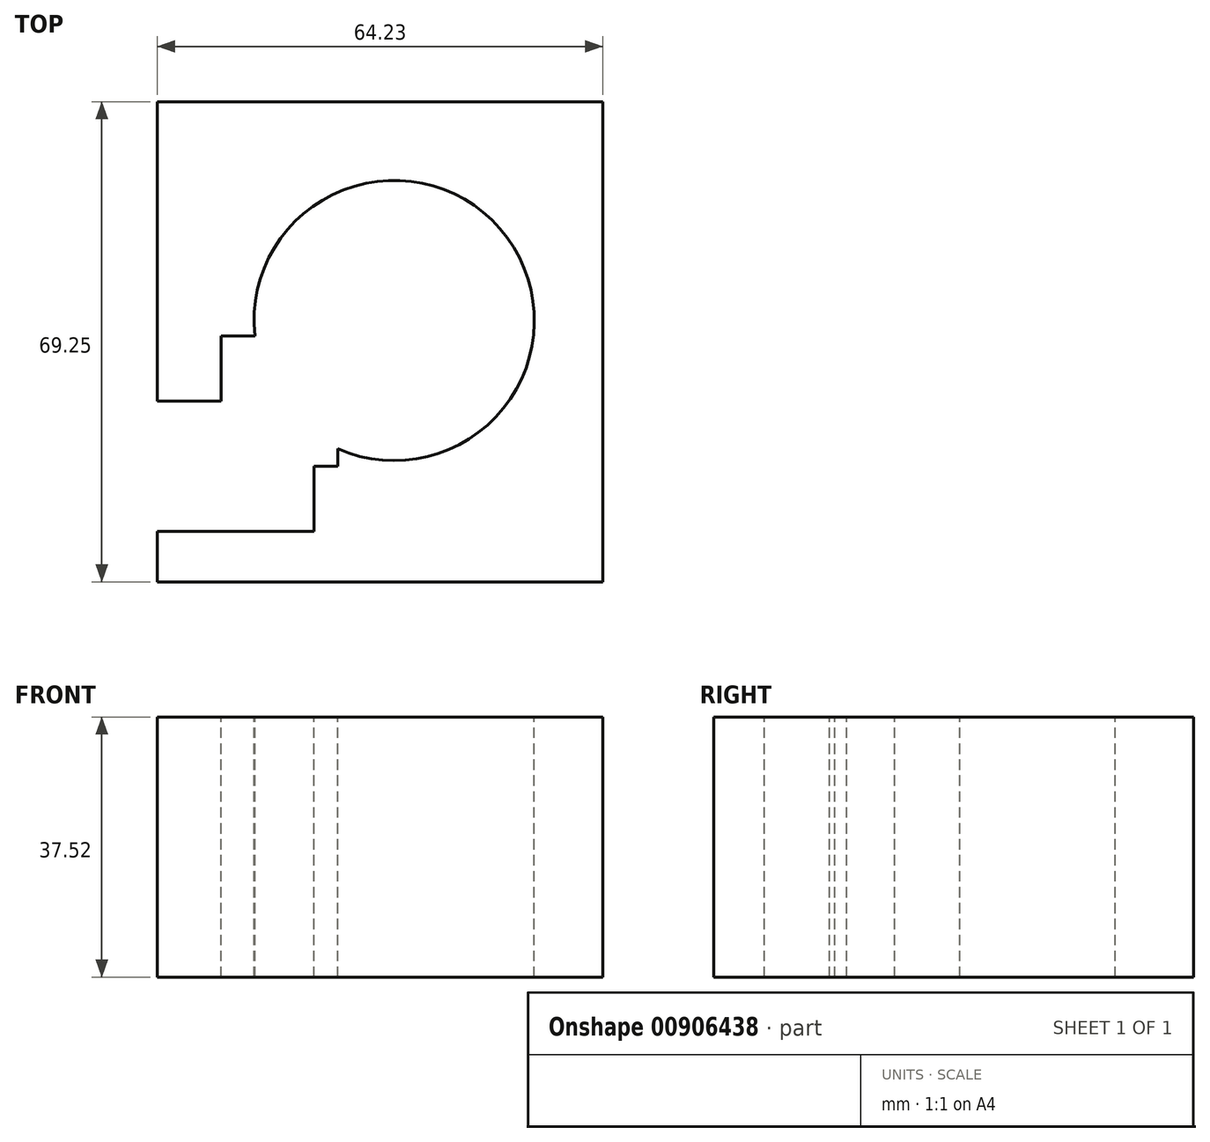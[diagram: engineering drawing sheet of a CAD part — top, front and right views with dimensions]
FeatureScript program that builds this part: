
annotation { "Feature Type Name" : "Feature", "Feature Type Description" : "" }
export const myFeature = defineFeature(function(context is Context, id is Id, definition is map)
    precondition{}
    {
        {
            var Q0;
            Q0=qCreatedBy(makeId("Top.planeOp"),FACE);
            var sketch = newSketch(context, id + "F0", { "sketchPlane" : qUnion([Q0])});
            skLineSegment(sketch, "E0.bottom", {"start": v(-34.15, 31.55) * mm, "end": v(30.08, 31.55) * mm});
            skLineSegment(sketch, "E0.top", {"start": v(-34.15, -37.7) * mm, "end": v(30.08, -37.7) * mm});
            skLineSegment(sketch, "E0.left", {"start": v(-34.15, 31.55) * mm, "end": v(-34.15, -37.7) * mm});
            skLineSegment(sketch, "E0.right", {"start": v(30.08, 31.55) * mm, "end": v(30.08, -37.7) * mm});
            skSolve(sketch);
        }
        {
            var Q0;
            Q0 = qSketchRegion(id + "F0", true);
            extrude(context, id + "F1", {"entities" : qUnion([Q0]), "depth" : 37.52 * mm, "offsetDistance" : 25.4 * mm});
        }
        {
            var Q0;
            Q0=makeQuery(id+"F1.opExtrude","CAP_FACE",FACE,{"disambiguationData":[OSD([sQuery(id+"F0.wireOp",EDGE,"E0.bottom"),sQuery(id+"F0.wireOp",EDGE,"E0.top"),sQuery(id+"F0.wireOp",EDGE,"E0.left"),sQuery(id+"F0.wireOp",EDGE,"E0.right")])],"isStart":false});
            var sketch = newSketch(context, id + "F2", { "sketchPlane" : qUnion([Q0])});
            skCircle(sketch, "E1", {"center": v(0, 0) * mm, "radius": 20.22 * mm});
            skSolve(sketch);
        }
        {
            var Q0;
            Q0 = qSketchRegion(id + "F2", true);
            extrude(context, id + "F3", {"entities" : qUnion([Q0]), "operationType" : NewBodyOperationType.REMOVE, "oppositeDirection" : true, "depth" : 93.56 * mm, "offsetDistance" : 25.4 * mm});
        }
        {
            var Q0;
            Q0=makeQuery(id+"F1.opExtrude","CAP_FACE",FACE,{"disambiguationData":[OSD([sQuery(id+"F0.wireOp",EDGE,"E0.bottom"),sQuery(id+"F0.wireOp",EDGE,"E0.top"),sQuery(id+"F0.wireOp",EDGE,"E0.left"),sQuery(id+"F0.wireOp",EDGE,"E0.right")])],"isStart":false});
            var sketch = newSketch(context, id + "F4", { "sketchPlane" : qUnion([Q0])});
            skLineSegment(sketch, "E2.bottom", {"start": v(-11.54, -30.39) * mm, "end": v(-38.41, -30.39) * mm});
            skLineSegment(sketch, "E2.top", {"start": v(-11.54, -11.6) * mm, "end": v(-38.41, -11.6) * mm});
            skLineSegment(sketch, "E2.left", {"start": v(-11.54, -30.39) * mm, "end": v(-11.54, -11.6) * mm});
            skLineSegment(sketch, "E2.right", {"start": v(-38.41, -30.39) * mm, "end": v(-38.41, -11.6) * mm});
            skPoint(sketch, "E2.middle", {"position": v(-24.98, -21) * mm});
            skLineSegment(sketch, "E3.bottom", {"start": v(-38.41, -21) * mm, "end": v(-11.54, -21) * mm});
            skLineSegment(sketch, "E3.top", {"start": v(-38.41, -21) * mm, "end": v(-11.54, -21) * mm});
            skLineSegment(sketch, "E3.left", {"start": v(-38.41, -21) * mm, "end": v(-38.41, -21) * mm});
            skLineSegment(sketch, "E3.right", {"start": v(-11.54, -21) * mm, "end": v(-11.54, -21) * mm});
            skLineSegment(sketch, "E4.bottom", {"start": v(-24.98, -30.39) * mm, "end": v(-24.98, -30.39) * mm});
            skLineSegment(sketch, "E4.top", {"start": v(-24.98, 7.2) * mm, "end": v(-24.98, 7.2) * mm});
            skLineSegment(sketch, "E4.left", {"start": v(-24.98, -30.39) * mm, "end": v(-24.98, 7.2) * mm});
            skLineSegment(sketch, "E4.right", {"start": v(-24.98, -30.39) * mm, "end": v(-24.98, 7.2) * mm});
            skPoint(sketch, "E4.middle", {"position": v(-24.98, -11.6) * mm});
            skLineSegment(sketch, "E5.bottom", {"start": v(-24.98, -21) * mm, "end": v(-8.15, -21) * mm});
            skLineSegment(sketch, "E5.top", {"start": v(-24.98, -2.2) * mm, "end": v(-8.15, -2.2) * mm});
            skLineSegment(sketch, "E5.left", {"start": v(-24.98, -21) * mm, "end": v(-24.98, -2.2) * mm});
            skLineSegment(sketch, "E5.right", {"start": v(-8.15, -21) * mm, "end": v(-8.15, -2.2) * mm});
            skPoint(sketch, "E5.middle", {"position": v(-16.56, -11.6) * mm});
            skSolve(sketch);
        }
        {
            var Q0;
            Q0 = qSketchRegion(id + "F4", true);
            extrude(context, id + "F5", {"entities" : qUnion([Q0]), "operationType" : NewBodyOperationType.REMOVE, "oppositeDirection" : true, "depth" : 134.1 * mm, "offsetDistance" : 25.4 * mm});
        }
    });
